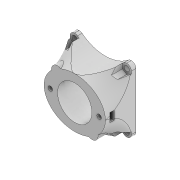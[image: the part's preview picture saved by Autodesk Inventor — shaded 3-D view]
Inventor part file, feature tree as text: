
AUTODESK INVENTOR PART (.ipt)
format: ipt  version: 2020 (Build 240168000, 168)  size: 660,992 bytes
history: native  units: mm
features: sketch x18, extrude x11, mirror x8, projected_geometry x7, other x4, sweep x3, fillet x2, revolve x2, plane x2, reference x2
ambient origin geometry x8: Origin, YZ Plane, XZ Plane, XY Plane, X Axis, Y Axis, Z Axis, Center Point
bodies: Body1 (feature_tree)
feature tree (59):
  extrude  "Extrusion3"  Depth=42.0mm
  extrude  "Extrusion4"  Depth=20.0mm
  fillet  "Fillet2"  Radius=3.0mm
  mirror  "Mirror2"
  mirror  "Mirror3"
  extrude  "Extrusion5"  TaperAngle=0.0deg  [1 undecoded]
  mirror  "Mirror4"
  fillet  "Fillet3"  Radius=3.0mm
  extrude  "Extrusion6"  Depth=1.5mm TaperAngle=0.0deg
  sketch  "Sketch8"  dims[d37=3.0mm d39=0.0mm d40=0.0mm]
  revolve  "Revolution1"  [1 undecoded]
  extrude  "Extrusion7"  Depth=11.0mm
  plane  "Work Plane1"
  extrude  "Extrusion8"  TaperAngle=90.0deg  [1 undecoded]
  mirror  "Mirror5"
  mirror  "Mirror6"
  extrude  "Extrusion9"  [1 undecoded]
  plane  "Work Plane2"
  extrude  "Extrusion10"  Depth=2.8mm TaperAngle=0.0deg
  mirror  "Mirror7"
  extrude  "Extrusion11"  Depth=3.0mm
  mirror  "Mirror8"
  mirror  "Mirror9"
  extrude  "Extrusion12"  [1 undecoded]
  sketch  "Sketch26"  dims[d57=2.8mm d58=0.0mm d59=10.0mm d60=0.0mm]
  sweep  "Sweep4"
  sweep  "Sweep5"
  sketch  "Sketch30"  dims[d93=0.0mm d94=0.0mm d96=0.0mm d97=0.0mm]
  sweep  "Sweep6"
  revolve  "Revolution2"  [1 undecoded]
  extrude  "Extrusion14"  Depth=20.0mm
  sketch  "Sketch3"  dims[d24=40.2mm d25=42.0mm]
  sketch  "Sketch4"  dims[d26=20.0mm d27=0.0mm d28=3.0mm d29=3.0mm]
  sketch  "Sketch5"  dims[d30=3.4mm d31=0.0mm d32=0.0mm d33=3.0mm]
  sketch  "Sketch7"  dims[d34=3.0mm d35=1.5mm d36=0.0mm]
  reference  "Reference1"
  projected_geometry  "Projected Loop1"
  sketch  "Sketch9"  dims[d41=18.0mm d42=11.0mm]
  sketch  "Sketch10"  dims[d43=0.25mm d44=90.0deg]
  sketch  "Sketch11"  dims[d45=0.5mm d46=0.0mm d47=-3.0mm]
  sketch  "Sketch12"  dims[d48=5.8mm d49=2.8mm d50=0.0mm]
  sketch  "Sketch13"  dims[d51=16.0mm d52=3.0mm]
  sketch  "Sketch14"  dims[d53=10.0mm d54=0.0mm d55=-3.0mm]
  projected_geometry  "Projected Loop12"
  sketch  "Sketch27"  dims[d61=0.5mm d62=0.0mm d87=1.1mm]
  sketch  "Sketch29"  dims[d88=1.1mm d92=25.0mm]
  sketch  "Sketch31"  dims[d98=20.0mm d99=20.0mm]
  projected_geometry  "Projected Loop13"
  sketch  "Sketch32"  dims[d100=0.0mm d101=0.0mm]
  projected_geometry  "Projected Loop14"
  projected_geometry  "Projected Loop15"
  sketch  "Sketch33"  dims[d102=90.0deg d103=8.0mm d104=8.0mm d105=10.0mm d106=0.0mm d111=5.0mm d112=5.8mm d113=10.0mm d67=0.5mm d68=0.872665mm d69=0.5mm d70=0.872665mm]
  reference  "Reference3"
  projected_geometry  "Projected Loop16"
  projected_geometry  "Projected Loop17"
  other  "<userpath>\Google Drive\Breathney\oxymount.iam"
  other  "oxymount.iam"
  other  "oxysens:1"
  other  "wall V2:1"
note: 6 required parameter values undecoded (feature->parameter linkage not recoverable at this tier; creation-order binding heuristic only, values carry confidence <= 0.55)